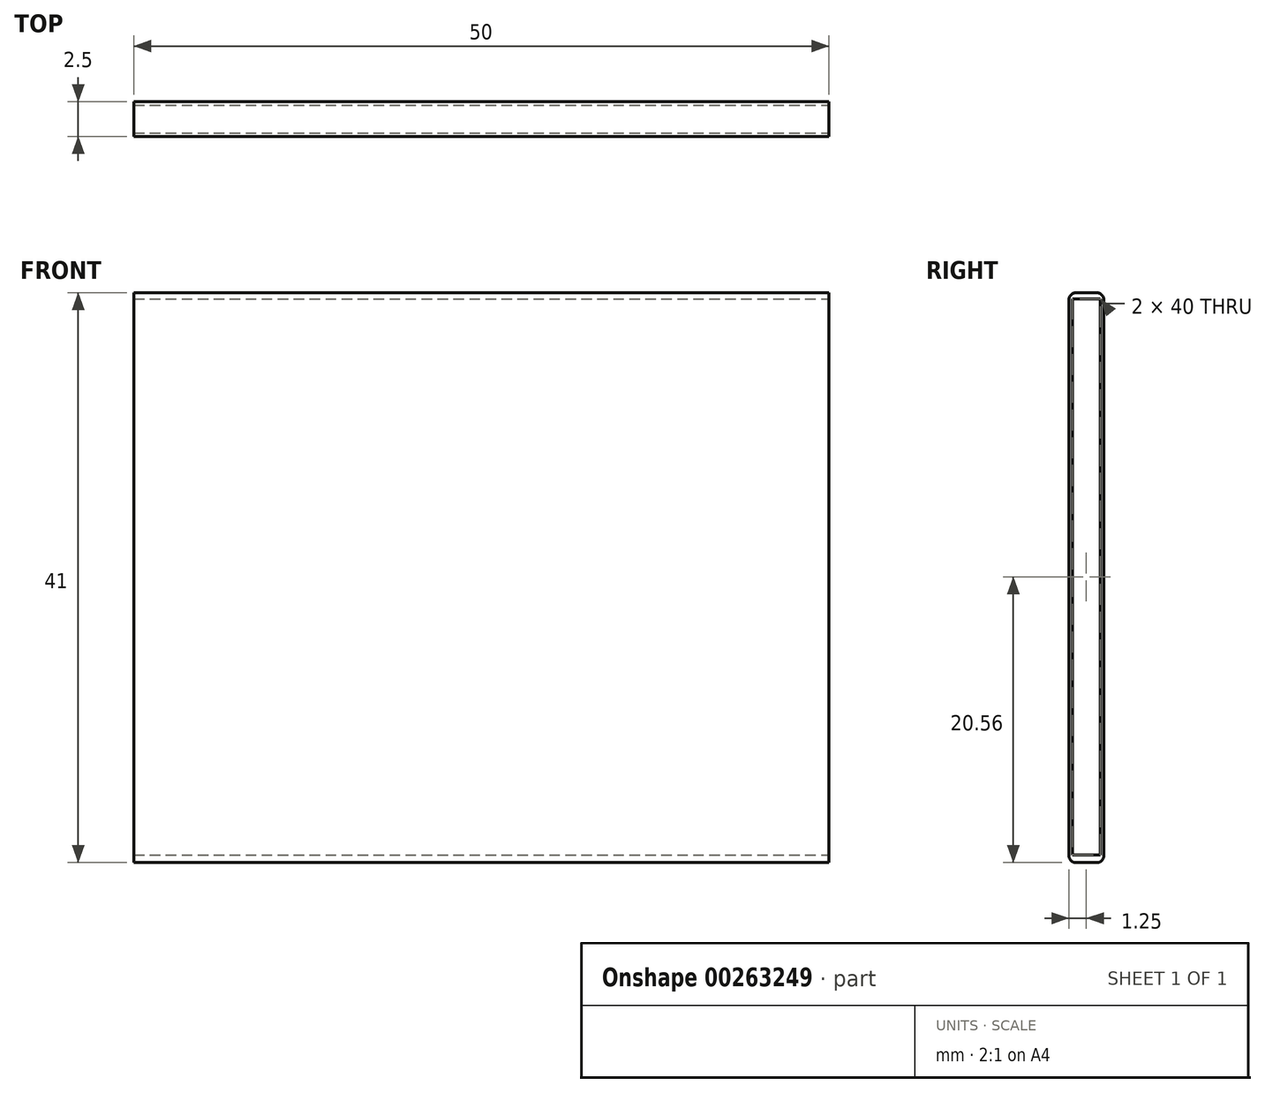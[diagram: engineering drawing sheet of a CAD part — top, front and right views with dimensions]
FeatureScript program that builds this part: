
annotation { "Feature Type Name" : "Feature", "Feature Type Description" : "" }
export const myFeature = defineFeature(function(context is Context, id is Id, definition is map)
    precondition{}
    {
        {
            var Q0;
            Q0=qCreatedBy(makeId("Right.planeOp"),FACE);
            var sketch = newSketch(context, id + "F0", { "sketchPlane" : qUnion([Q0])});
            skLineSegment(sketch, "E0", {"start": v(1, 0) * mm, "end": v(1, 20) * mm});
            skLineSegment(sketch, "E1", {"start": v(1, 20) * mm, "end": v(-1, 20) * mm});
            skLineSegment(sketch, "E2", {"start": v(-1, 20) * mm, "end": v(-1, -20) * mm});
            skLineSegment(sketch, "E3", {"start": v(-1, -20) * mm, "end": v(1, -20) * mm});
            skLineSegment(sketch, "E4", {"start": v(1, -20) * mm, "end": v(1, 0) * mm});
            skSolve(sketch);
        }
        {
            var Q0;
            Q0=qCreatedBy(makeId("Right.planeOp"),FACE);
            var sketch = newSketch(context, id + "F1", { "sketchPlane" : qUnion([Q0])});
            skLineSegment(sketch, "E5", {"start": v(1.25, -20.06) * mm, "end": v(1.25, 19.94) * mm});
            skLineSegment(sketch, "E6", {"start": v(0.75, 20.44) * mm, "end": v(-0.75, 20.44) * mm});
            skLineSegment(sketch, "E7", {"start": v(-1.25, 19.94) * mm, "end": v(-1.25, -20.06) * mm});
            skLineSegment(sketch, "E8", {"start": v(-0.75, -20.56) * mm, "end": v(0.75, -20.56) * mm});
            skPoint(sketch, "E9.visualSharp", {"position": v(-1.25, 20.44) * mm});
            skArc(sketch, "E9.filletArc", {"start": v(-0.75, 20.44) * mm, "mid": v(-1.1, 20.3) * mm, "end": v(-1.25, 19.94) * mm});
            skPoint(sketch, "E10.visualSharp", {"position": v(1.25, 20.44) * mm});
            skArc(sketch, "E10.filletArc", {"start": v(1.25, 19.94) * mm, "mid": v(1.1, 20.3) * mm, "end": v(0.75, 20.44) * mm});
            skPoint(sketch, "E11.visualSharp", {"position": v(-1.25, -20.56) * mm});
            skArc(sketch, "E11.filletArc", {"start": v(-1.25, -20.06) * mm, "mid": v(-1.1, -20.42) * mm, "end": v(-0.75, -20.56) * mm});
            skPoint(sketch, "E12.visualSharp", {"position": v(1.25, -20.56) * mm});
            skArc(sketch, "E12.filletArc", {"start": v(0.75, -20.56) * mm, "mid": v(1.1, -20.42) * mm, "end": v(1.25, -20.06) * mm});
            skSolve(sketch);
        }
        {
            var Q0;
            Q0=makeQuery(id+"F1.imprint","IMPRINT",FACE,{"disambiguationData":[TD([[makeQuery(id+"F1.imprint","IMPRINT",EDGE,{"derivedFrom":sQuery(id+"F1.wireOp",EDGE,"E5")}),1.0]])]});
            extrude(context, id + "F2", {"entities" : qUnion([Q0]), "oppositeDirection" : true, "depth" : 50 * mm});
        }
        {
            var Q0;
            Q0=makeQuery(id+"F0.imprint","IMPRINT",FACE,{"disambiguationData":[TD([[makeQuery(id+"F0.imprint","IMPRINT",EDGE,{"derivedFrom":sQuery(id+"F0.wireOp",EDGE,"E0")}),1.0]])]});
            extrude(context, id + "F3", {"entities" : qUnion([Q0]), "operationType" : NewBodyOperationType.REMOVE, "endBound" : BoundingType.THROUGH_ALL, "oppositeDirection" : true, "depth" : 25 * mm});
        }
    });
